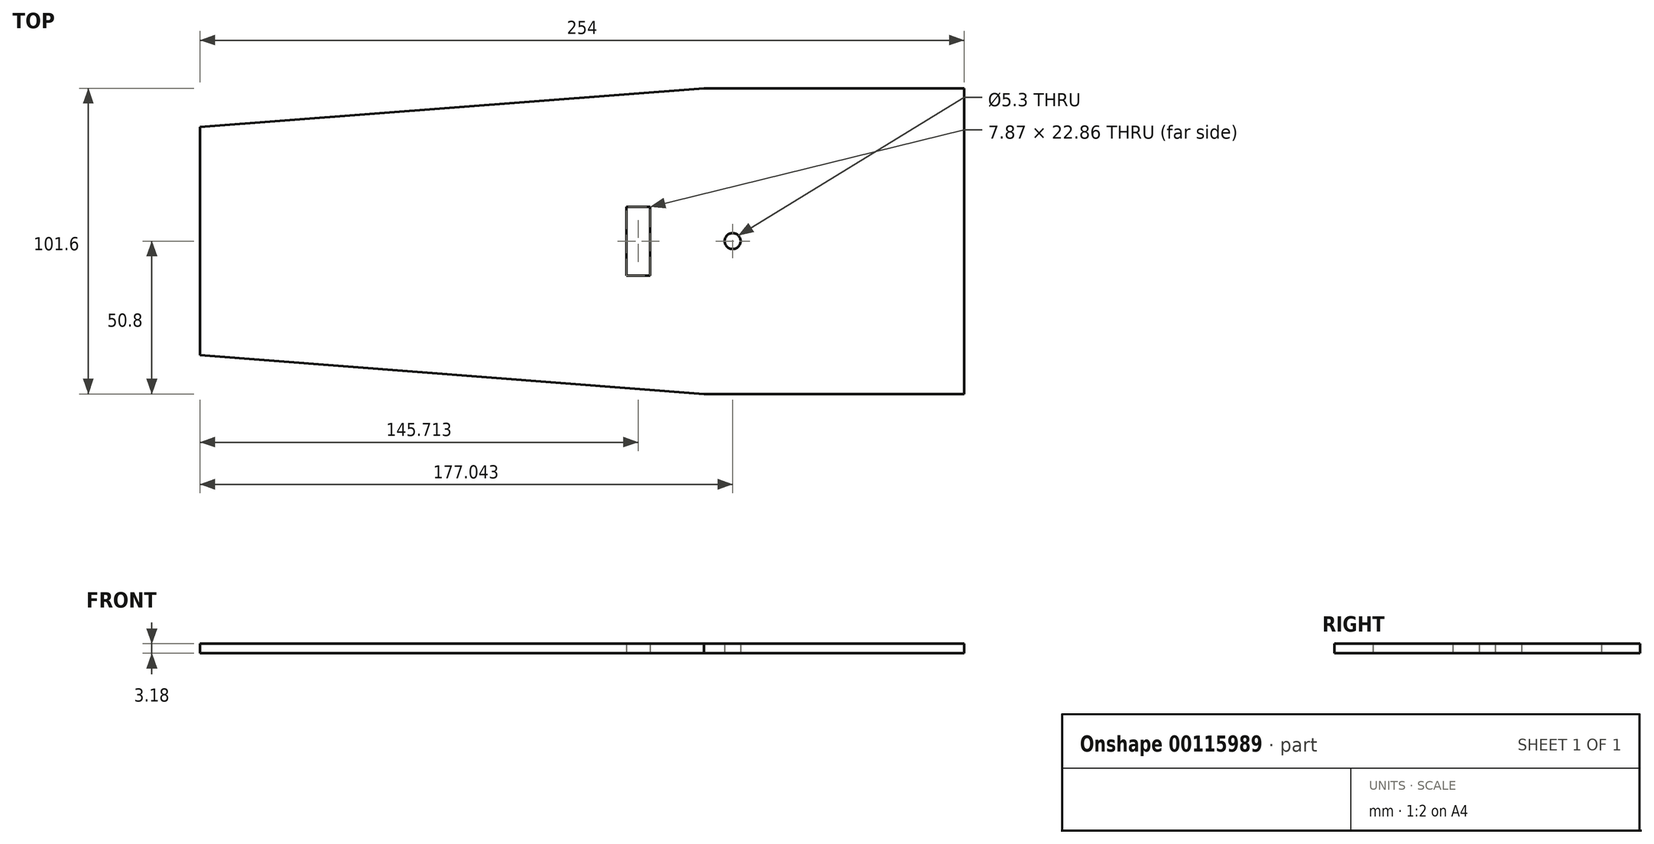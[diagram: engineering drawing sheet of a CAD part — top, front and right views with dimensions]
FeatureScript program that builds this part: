
annotation { "Feature Type Name" : "Feature", "Feature Type Description" : "" }
export const myFeature = defineFeature(function(context is Context, id is Id, definition is map)
    precondition{}
    {
        {
            var Q0;
            Q0=qCreatedBy(makeId("Top.planeOp"),FACE);
            var sketch = newSketch(context, id + "F0", { "sketchPlane" : qUnion([Q0])});
            skLineSegment(sketch, "E0", {"start": v(46.28, 50.8) * mm, "end": v(-121.26, 37.95) * mm});
            skLineSegment(sketch, "E1.MirrorCS", {"start": v(46.28, -50.8) * mm, "end": v(-121.26, -37.95) * mm});
            skLineSegment(sketch, "E2.bottom", {"start": v(46.28, 50.8) * mm, "end": v(132.74, 50.8) * mm});
            skLineSegment(sketch, "E2.top", {"start": v(46.28, -50.8) * mm, "end": v(132.74, -50.8) * mm});
            skLineSegment(sketch, "E2.right", {"start": v(132.74, 50.8) * mm, "end": v(132.74, -50.8) * mm});
            skCircle(sketch, "E3", {"center": v(55.78, 0) * mm, "radius": 2.65 * mm});
            skLineSegment(sketch, "E4", {"start": v(-121.26, 37.95) * mm, "end": v(-121.26, -37.95) * mm});
            skLineSegment(sketch, "E5", {"start": v(55.78, -2.65) * mm, "end": v(55.78, 2.65) * mm, "construction": true});
            skLineSegment(sketch, "E6.bottom", {"start": v(20.52, -11.43) * mm, "end": v(28.39, -11.43) * mm});
            skLineSegment(sketch, "E6.top", {"start": v(20.52, 11.43) * mm, "end": v(28.39, 11.43) * mm});
            skLineSegment(sketch, "E6.left", {"start": v(20.52, -11.43) * mm, "end": v(20.52, 11.43) * mm});
            skLineSegment(sketch, "E6.right", {"start": v(28.39, -11.43) * mm, "end": v(28.39, 11.43) * mm});
            skPoint(sketch, "E6.middle", {"position": v(24.45, 0) * mm});
            skSolve(sketch);
        }
        {
            var Q0;
            Q0=makeQuery(id+"F0.imprint","IMPRINT",FACE,{"disambiguationData":[TD([[makeQuery(id+"F0.imprint","IMPRINT",EDGE,{"derivedFrom":sQuery(id+"F0.wireOp",EDGE,"E0")}),1.0]])]});
            extrude(context, id + "F1", {"entities" : qUnion([Q0]), "depth" : 3.17 * mm});
        }
    });
